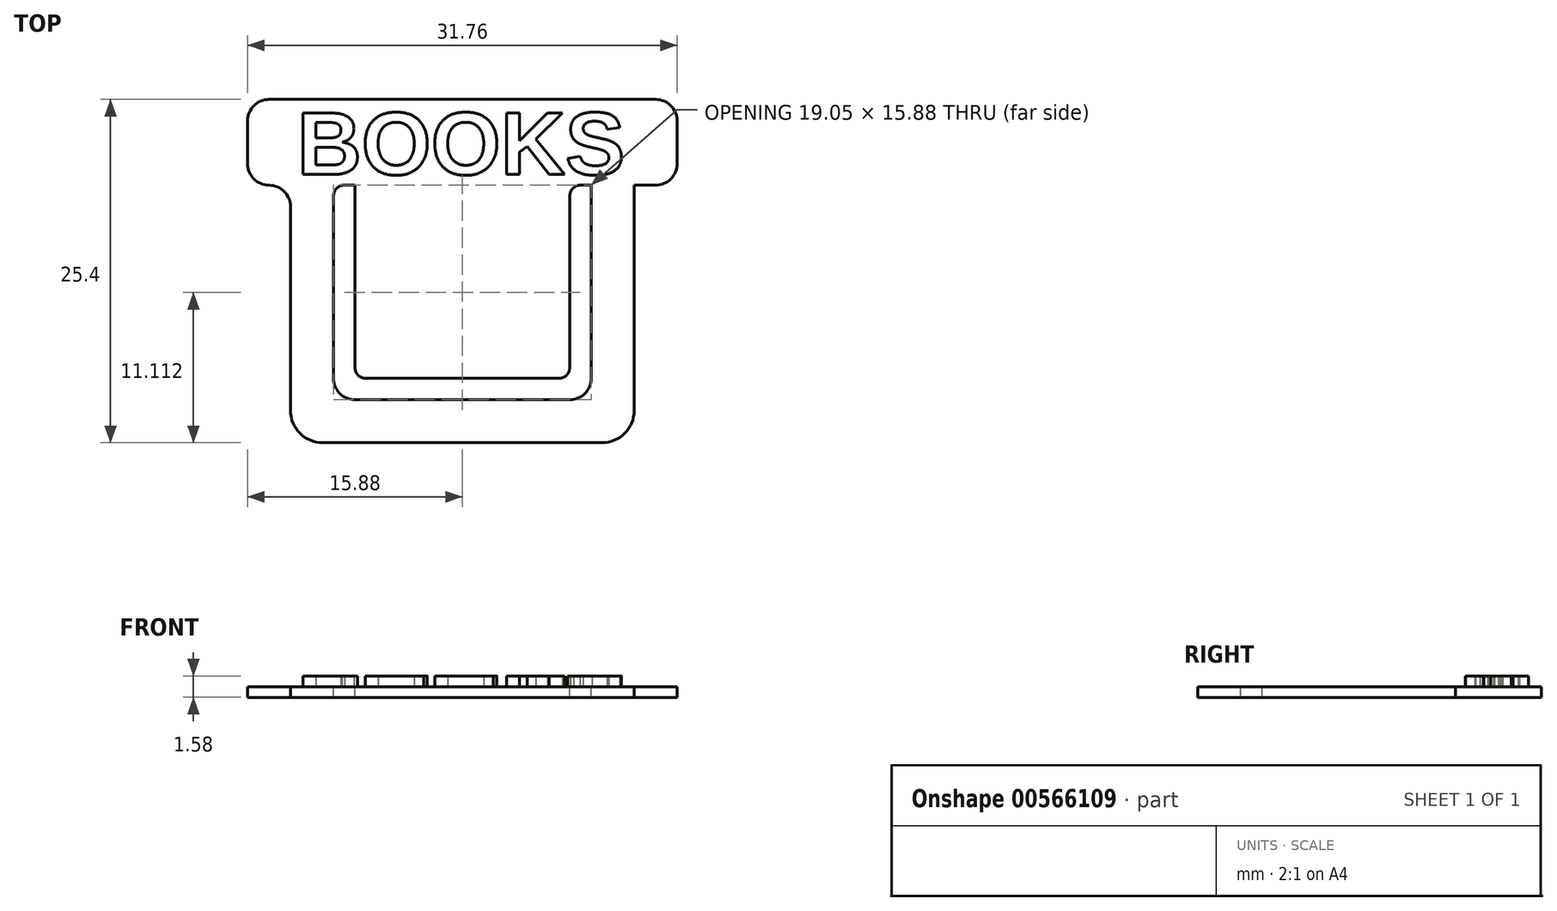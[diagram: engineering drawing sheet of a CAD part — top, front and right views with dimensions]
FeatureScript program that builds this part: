
annotation { "Feature Type Name" : "Feature", "Feature Type Description" : "" }
export const myFeature = defineFeature(function(context is Context, id is Id, definition is map)
    precondition{}
    {
        {
            var Q0;
            Q0=qCreatedBy(makeId("Front.planeOp"),FACE);
            var sketch = newSketch(context, id + "F0", { "sketchPlane" : qUnion([Q0])});
            skLineSegment(sketch, "E0.bottom", {"start": v(12.7, 9.53) * mm, "end": v(-12.7, 9.53) * mm});
            skLineSegment(sketch, "E0.top", {"start": v(12.7, -9.53) * mm, "end": v(-12.7, -9.53) * mm});
            skLineSegment(sketch, "E0.left", {"start": v(12.7, 9.53) * mm, "end": v(12.7, -9.53) * mm});
            skLineSegment(sketch, "E0.right", {"start": v(-12.7, 9.53) * mm, "end": v(-12.7, -9.53) * mm});
            skPoint(sketch, "E0.middle", {"position": v(0, 0) * mm});
            skSolve(sketch);
        }
        {
            var Q0;
            Q0=makeQuery(id+"F0.imprint","IMPRINT",FACE,{"disambiguationData":[TD([[makeQuery(id+"F0.imprint","IMPRINT",EDGE,{"derivedFrom":sQuery(id+"F0.wireOp",EDGE,"E0.bottom")}),1.0]])]});
            extrude(context, id + "F1", {"entities" : qUnion([Q0]), "depth" : 0.8 * mm, "offsetDistance" : 25.4 * mm});
        }
        {
            var Q0;
            Q0=makeQuery(id+"F1.opExtrude","SWEPT_EDGE",EDGE,{"disambiguationData":[OSD([sQuery(id+"F0.wireOp",EDGE,"E0.top"),sQuery(id+"F0.wireOp",EDGE,"E0.left")])]});
            var Q1;
            Q1=makeQuery(id+"F1.opExtrude","SWEPT_EDGE",EDGE,{"disambiguationData":[OSD([sQuery(id+"F0.wireOp",EDGE,"E0.top"),sQuery(id+"F0.wireOp",EDGE,"E0.right")])]});
            fillet(context, id + "F2", {"entities" : qUnion([Q0, Q1]), "radius" : 2.38 * mm, "tangentPropagation" : true, "allowEdgeOverflow" : false});
        }
        {
            var Q0;
            Q0=makeQuery(id+"F1.opExtrude","CAP_FACE",FACE,{"disambiguationData":[OSD([sQuery(id+"F0.wireOp",EDGE,"E0.bottom"),sQuery(id+"F0.wireOp",EDGE,"E0.top"),sQuery(id+"F0.wireOp",EDGE,"E0.left"),sQuery(id+"F0.wireOp",EDGE,"E0.right")])],"isStart":false});
            var sketch = newSketch(context, id + "F3", { "sketchPlane" : qUnion([Q0])});
            skLineSegment(sketch, "E1.bottom", {"start": v(9.52, 9.53) * mm, "end": v(-9.53, 9.53) * mm});
            skLineSegment(sketch, "E1.top", {"start": v(9.53, -6.35) * mm, "end": v(-9.53, -6.35) * mm});
            skLineSegment(sketch, "E1.left", {"start": v(9.52, 9.53) * mm, "end": v(9.53, -6.35) * mm});
            skLineSegment(sketch, "E1.right", {"start": v(-9.53, 9.53) * mm, "end": v(-9.52, -6.35) * mm});
            skPoint(sketch, "E1.middle", {"position": v(0, 0) * mm});
            skSolve(sketch);
        }
        {
            var Q0;
            Q0=makeQuery(id+"F3.imprint","IMPRINT",FACE,{"disambiguationData":[TD([[makeQuery(id+"F3.imprint","IMPRINT",EDGE,{"derivedFrom":sQuery(id+"F3.wireOp",EDGE,"E1.bottom")}),1.0]])]});
            extrude(context, id + "F4", {"entities" : qUnion([Q0]), "operationType" : NewBodyOperationType.REMOVE, "oppositeDirection" : true, "depth" : 4.93 * mm, "offsetDistance" : 25.4 * mm});
        }
        {
            var Q0;
            Q0=makeQuery(id+"F1.opExtrude","CAP_FACE",FACE,{"disambiguationData":[OSD([sQuery(id+"F0.wireOp",EDGE,"E0.bottom"),sQuery(id+"F0.wireOp",EDGE,"E0.top"),sQuery(id+"F0.wireOp",EDGE,"E0.left"),sQuery(id+"F0.wireOp",EDGE,"E0.right")])],"isStart":false});
            var sketch = newSketch(context, id + "F5", { "sketchPlane" : qUnion([Q0])});
            skLineSegment(sketch, "E2.bottom", {"start": v(-15.88, 9.53) * mm, "end": v(15.87, 9.53) * mm});
            skLineSegment(sketch, "E2.top", {"start": v(-15.88, 15.88) * mm, "end": v(15.87, 15.88) * mm});
            skLineSegment(sketch, "E2.left", {"start": v(-15.88, 9.53) * mm, "end": v(-15.88, 15.88) * mm});
            skLineSegment(sketch, "E2.right", {"start": v(15.87, 9.53) * mm, "end": v(15.87, 15.88) * mm});
            skSolve(sketch);
        }
        {
            var Q0;
            Q0=makeQuery(id+"F5.imprint","IMPRINT",FACE,{"disambiguationData":[TD([[makeQuery(id+"F5.imprint","IMPRINT",EDGE,{"derivedFrom":sQuery(id+"F5.wireOp",EDGE,"E2.top")}),-1.0]])]});
            extrude(context, id + "F6", {"entities" : qUnion([Q0]), "operationType" : NewBodyOperationType.ADD, "oppositeDirection" : true, "depth" : 0.8 * mm, "offsetDistance" : 25.4 * mm});
        }
        {
            var Q0;
            Q0=makeQuery(id+"F6.opExtrude","SWEPT_EDGE",EDGE,{"disambiguationData":[OSD([sQuery(id+"F5.wireOp",EDGE,"E2.top"),sQuery(id+"F5.wireOp",EDGE,"E2.left")])]});
            var Q1;
            Q1=makeQuery(id+"F6.opExtrude","SWEPT_EDGE",EDGE,{"disambiguationData":[OSD([sQuery(id+"F5.wireOp",EDGE,"E2.top"),sQuery(id+"F5.wireOp",EDGE,"E2.right")])]});
            var Q2;
            Q2=makeQuery(id+"F6.opExtrude","SWEPT_EDGE",EDGE,{"disambiguationData":[OSD([sQuery(id+"F5.wireOp",EDGE,"E2.bottom"),sQuery(id+"F5.wireOp",EDGE,"E2.right")])]});
            var Q3;
            Q3=makeQuery(id+"F1.opExtrude","SWEPT_EDGE",EDGE,{"disambiguationData":[OSD([sQuery(id+"F0.wireOp",EDGE,"E0.bottom"),sQuery(id+"F0.wireOp",EDGE,"E0.left")])]});
            var Q4;
            Q4=makeQuery(id+"F6.opExtrude","SWEPT_EDGE",EDGE,{"disambiguationData":[OSD([sQuery(id+"F5.wireOp",EDGE,"E2.bottom"),sQuery(id+"F5.wireOp",EDGE,"E2.left")])]});
            var Q5;
            Q5=makeQuery(id+"F1.opExtrude","SWEPT_EDGE",EDGE,{"disambiguationData":[OSD([sQuery(id+"F0.wireOp",EDGE,"E0.bottom"),sQuery(id+"F0.wireOp",EDGE,"E0.right")])]});
            fillet(context, id + "F7", {"entities" : qUnion([Q0, Q1, Q2, Q3, Q4, Q5]), "radius" : 1.59 * mm, "tangentPropagation" : true, "allowEdgeOverflow" : false});
        }
        {
            var Q0;
            Q0=makeQuery(id+"F4.boolean.opBoolean","COPY",EDGE,{"derivedFrom":makeQuery(id+"F4.opExtrude","SWEPT_EDGE",EDGE,{"disambiguationData":[OSD([sQuery(id+"F3.wireOp",EDGE,"E1.top"),sQuery(id+"F3.wireOp",EDGE,"E1.right")])]})});
            var Q1;
            Q1=makeQuery(id+"F4.boolean.opBoolean","COPY",EDGE,{"derivedFrom":makeQuery(id+"F4.opExtrude","SWEPT_EDGE",EDGE,{"disambiguationData":[OSD([sQuery(id+"F3.wireOp",EDGE,"E1.top"),sQuery(id+"F3.wireOp",EDGE,"E1.left")])]})});
            fillet(context, id + "F8", {"entities" : qUnion([Q0, Q1]), "radius" : 1.59 * mm, "tangentPropagation" : true, "allowEdgeOverflow" : false});
        }
        {
            var Q0;
            Q0=makeQuery(id+"F6.boolean.opBoolean","MERGE",FACE,{"derivedFrom":[makeQuery(id+"F1.opExtrude","CAP_FACE",FACE,{"disambiguationData":[OSD([sQuery(id+"F0.wireOp",EDGE,"E0.bottom"),sQuery(id+"F0.wireOp",EDGE,"E0.top"),sQuery(id+"F0.wireOp",EDGE,"E0.left"),sQuery(id+"F0.wireOp",EDGE,"E0.right")])],"isStart":false}),makeQuery(id+"F6.opExtrude","CAP_FACE",FACE,{"disambiguationData":[OSD([sQuery(id+"F5.wireOp",EDGE,"E2.bottom"),sQuery(id+"F5.wireOp",EDGE,"E2.top"),sQuery(id+"F5.wireOp",EDGE,"E2.left"),sQuery(id+"F5.wireOp",EDGE,"E2.right")])],"isStart":true})]});
            var sketch = newSketch(context, id + "F9", { "sketchPlane" : qUnion([Q0])});
            skLineSegment(sketch, "E3.bottom", {"start": v(-7.94, 9.53) * mm, "end": v(7.94, 9.53) * mm});
            skLineSegment(sketch, "E3.top", {"start": v(-7.94, -4.76) * mm, "end": v(7.94, -4.76) * mm});
            skLineSegment(sketch, "E3.left", {"start": v(-7.94, 9.53) * mm, "end": v(-7.94, -4.76) * mm});
            skLineSegment(sketch, "E3.right", {"start": v(7.94, 9.53) * mm, "end": v(7.94, -4.76) * mm});
            skSolve(sketch);
        }
        {
            var Q0;
            Q0=makeQuery(id+"F9.imprint","IMPRINT",FACE,{"disambiguationData":[TD([[makeQuery(id+"F9.imprint","IMPRINT",EDGE,{"derivedFrom":sQuery(id+"F9.wireOp",EDGE,"E3.bottom")}),1.0]])]});
            extrude(context, id + "F10", {"entities" : qUnion([Q0]), "operationType" : NewBodyOperationType.ADD, "oppositeDirection" : true, "depth" : 0.8 * mm, "offsetDistance" : 25.4 * mm});
        }
        {
            var Q0;
            Q0=makeQuery(id+"F10.boolean.opBoolean","MERGE",FACE,{"derivedFrom":[makeQuery(id+"F6.boolean.opBoolean","MERGE",FACE,{"derivedFrom":[makeQuery(id+"F1.opExtrude","CAP_FACE",FACE,{"disambiguationData":[OSD([sQuery(id+"F0.wireOp",EDGE,"E0.bottom"),sQuery(id+"F0.wireOp",EDGE,"E0.top"),sQuery(id+"F0.wireOp",EDGE,"E0.left"),sQuery(id+"F0.wireOp",EDGE,"E0.right")])],"isStart":false}),makeQuery(id+"F6.opExtrude","CAP_FACE",FACE,{"disambiguationData":[OSD([sQuery(id+"F5.wireOp",EDGE,"E2.bottom"),sQuery(id+"F5.wireOp",EDGE,"E2.top"),sQuery(id+"F5.wireOp",EDGE,"E2.left"),sQuery(id+"F5.wireOp",EDGE,"E2.right")])],"isStart":true})]}),makeQuery(id+"F10.opExtrude","CAP_FACE",FACE,{"disambiguationData":[OSD([sQuery(id+"F9.wireOp",EDGE,"E3.bottom"),sQuery(id+"F9.wireOp",EDGE,"E3.top"),sQuery(id+"F9.wireOp",EDGE,"E3.left"),sQuery(id+"F9.wireOp",EDGE,"E3.right")])],"isStart":true})]});
            var sketch = newSketch(context, id + "F11", { "sketchPlane" : qUnion([Q0])});
            skText(sketch, "E4", { "text": "BOOKS", "fontName": "Arimo-Bold.ttf"});
            const initialGuessF11  = {"E4": [-0.01223, 0.01032, 1, 0, 0.00476]};
            skSetInitialGuess(sketch, initialGuessF11);
            skSolve(sketch);
        }
        {
            var Q0;
            Q0=makeQuery(id+"F11.imprint","IMPRINT",FACE,{"disambiguationData":[TD([[makeQuery(id+"F11.imprint","IMPRINT",EDGE,{"derivedFrom":sQuery(id+"F11.wireOp",EDGE,"E4.sketch_text.stroke-0")}),-1.0]])]});
            var Q1;
            Q1=makeQuery(id+"F11.imprint","IMPRINT",FACE,{"disambiguationData":[TD([[makeQuery(id+"F11.imprint","IMPRINT",EDGE,{"derivedFrom":sQuery(id+"F11.wireOp",EDGE,"E4.sketch_text.stroke-8")}),-1.0]])]});
            var Q2;
            Q2=makeQuery(id+"F11.imprint","IMPRINT",FACE,{"disambiguationData":[TD([[makeQuery(id+"F11.imprint","IMPRINT",EDGE,{"derivedFrom":sQuery(id+"F11.wireOp",EDGE,"E4.sketch_text.stroke-25")}),-1.0]])]});
            var Q3;
            Q3=makeQuery(id+"F11.imprint","IMPRINT",FACE,{"disambiguationData":[TD([[makeQuery(id+"F11.imprint","IMPRINT",EDGE,{"derivedFrom":sQuery(id+"F11.wireOp",EDGE,"E4.sketch_text.stroke-40")}),-1.0]])]});
            var Q4;
            Q4=makeQuery(id+"F11.imprint","IMPRINT",FACE,{"disambiguationData":[TD([[makeQuery(id+"F11.imprint","IMPRINT",EDGE,{"derivedFrom":sQuery(id+"F11.wireOp",EDGE,"E4.sketch_text.stroke-55")}),-1.0]])]});
            var Q5;
            Q5=makeQuery(id+"F11.imprint","IMPRINT",FACE,{"disambiguationData":[TD([[makeQuery(id+"F11.imprint","IMPRINT",EDGE,{"derivedFrom":sQuery(id+"F11.wireOp",EDGE,"E4.sketch_text.stroke-58")}),-1.0]])]});
            var Q6;
            Q6=makeQuery(id+"F11.imprint","IMPRINT",FACE,{"disambiguationData":[TD([[makeQuery(id+"F11.imprint","IMPRINT",EDGE,{"derivedFrom":sQuery(id+"F11.wireOp",EDGE,"E4.sketch_text.stroke-70")}),-1.0]])]});
            extrude(context, id + "F12", {"entities" : qUnion([Q0, Q1, Q2, Q3, Q4, Q5, Q6]), "operationType" : NewBodyOperationType.ADD, "depth" : 0.8 * mm, "offsetDistance" : 25.4 * mm});
        }
        {
            var Q0;
            Q0=makeQuery(id+"F10.opExtrude","SWEPT_EDGE",EDGE,{"disambiguationData":[OSD([sQuery(id+"F5.wireOp",EDGE,"E2.bottom"),sQuery(id+"F9.wireOp",EDGE,"E3.bottom"),sQuery(id+"F9.wireOp",EDGE,"E3.left")])]});
            var Q1;
            Q1=makeQuery(id+"F4.boolean.opBoolean","COPY",EDGE,{"derivedFrom":makeQuery(id+"F4.opExtrude","SWEPT_EDGE",EDGE,{"disambiguationData":[OSD([sQuery(id+"F0.wireOp",EDGE,"E0.bottom"),sQuery(id+"F3.wireOp",EDGE,"E1.bottom"),sQuery(id+"F3.wireOp",EDGE,"E1.right")])]})});
            var Q2;
            Q2=makeQuery(id+"F10.opExtrude","SWEPT_EDGE",EDGE,{"disambiguationData":[OSD([sQuery(id+"F5.wireOp",EDGE,"E2.bottom"),sQuery(id+"F9.wireOp",EDGE,"E3.bottom"),sQuery(id+"F9.wireOp",EDGE,"E3.right")])]});
            var Q3;
            Q3=makeQuery(id+"F4.boolean.opBoolean","COPY",EDGE,{"derivedFrom":makeQuery(id+"F4.opExtrude","SWEPT_EDGE",EDGE,{"disambiguationData":[OSD([sQuery(id+"F0.wireOp",EDGE,"E0.bottom"),sQuery(id+"F3.wireOp",EDGE,"E1.bottom"),sQuery(id+"F3.wireOp",EDGE,"E1.left")])]})});
            fillet(context, id + "F13", {"entities" : qUnion([Q0, Q1, Q2, Q3]), "radius" : 0.8 * mm, "tangentPropagation" : true, "allowEdgeOverflow" : false});
        }
        {
            var Q0;
            Q0=makeQuery(id+"F10.opExtrude","SWEPT_EDGE",EDGE,{"disambiguationData":[OSD([sQuery(id+"F9.wireOp",EDGE,"E3.top"),sQuery(id+"F9.wireOp",EDGE,"E3.left")])]});
            var Q1;
            Q1=makeQuery(id+"F10.opExtrude","SWEPT_EDGE",EDGE,{"disambiguationData":[OSD([sQuery(id+"F9.wireOp",EDGE,"E3.top"),sQuery(id+"F9.wireOp",EDGE,"E3.right")])]});
            fillet(context, id + "F14", {"entities" : qUnion([Q0, Q1]), "radius" : 0.8 * mm, "tangentPropagation" : true, "allowEdgeOverflow" : false});
        }
        {
            var Q0;
            Q0=makeQuery(id+"F1.opExtrude","SWEPT_BODY",BODY,{"disambiguationData":[OSD([sQuery(id+"F0.wireOp",EDGE,"E0.bottom"),sQuery(id+"F0.wireOp",EDGE,"E0.top"),sQuery(id+"F0.wireOp",EDGE,"E0.left"),sQuery(id+"F0.wireOp",EDGE,"E0.right")])]});
            var Q1;
            Q1=makeQuery(id+"F6.opExtrude","CAP_EDGE",EDGE,{"disambiguationData":[OSD([sQuery(id+"F5.wireOp",EDGE,"E2.top")])],"isStart":false});
            transform(context, id + "F15", {"entities" : qUnion([Q0]), "transformType" : TransformType.ROTATION, "transformAxis" : qUnion([Q1]), "angle" : 270 * degree, "makeCopy" : false});
        }
    });
